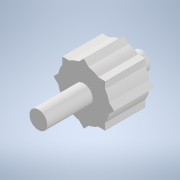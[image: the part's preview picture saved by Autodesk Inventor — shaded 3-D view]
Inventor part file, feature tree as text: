
AUTODESK INVENTOR PART (.ipt)
format: ipt  version: 2022.3 (Build 263350000, 350)  size: 145,920 bytes
history: native  units: mm
features: extrude x3, sketch x3, reference x2, other x2
ambient origin geometry x8: Origin, YZ Plane, XZ Plane, XY Plane, X Axis, Y Axis, Z Axis, Center Point
bodies: Solid1 (feature_tree)
feature tree (10):
  extrude  "Extrusion1"  Depth=5.1mm TaperAngle=0.0deg
  extrude  "Extrusion2"  Depth=2.0mm
  extrude  "Extrusion3"  Depth=2.0mm TaperAngle=360.0deg
  sketch  "Sketch1"  dims[d0=2.0mm d1=5.1mm d2=0.0mm]
  reference  "Reference1"
  sketch  "Sketch2"  dims[d3=1.2mm d4=2.0mm]
  reference  "Reference2"
  sketch  "Sketch3"  dims[d5=0.5mm d6=80.0mm d8=360.0deg d10=4.5mm d11=0.0mm d12=2.0mm d13=0.0mm]
  other  "Assembly3"
  other  "bok:1"
